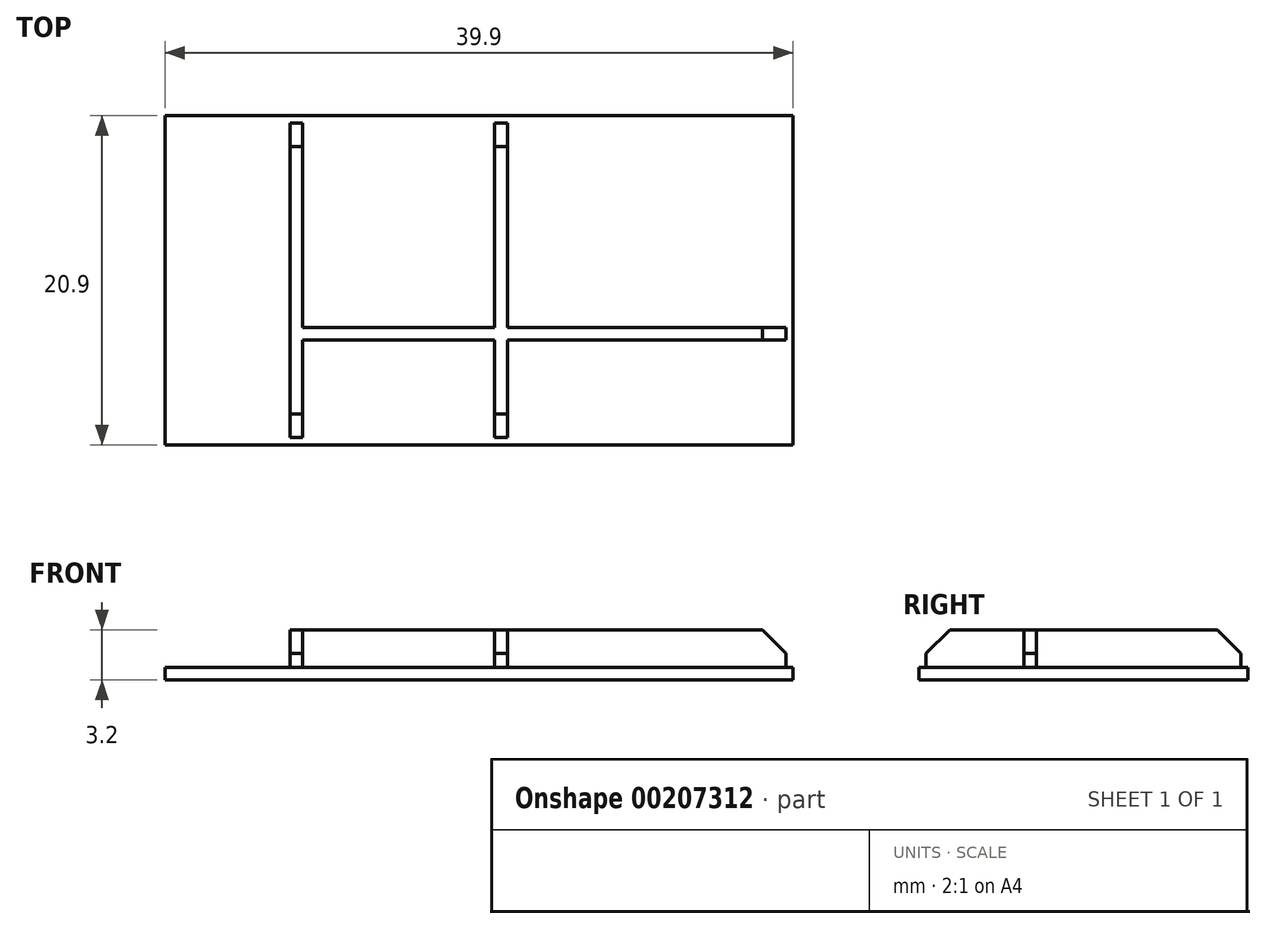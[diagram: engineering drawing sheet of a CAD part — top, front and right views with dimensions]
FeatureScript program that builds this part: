
annotation { "Feature Type Name" : "Feature", "Feature Type Description" : "" }
export const myFeature = defineFeature(function(context is Context, id is Id, definition is map)
    precondition{}
    {
        {
            var Q0;
            Q0=qCreatedBy(makeId("Top.planeOp"),FACE);
            var sketch = newSketch(context, id + "F0", { "sketchPlane" : qUnion([Q0])});
            skLineSegment(sketch, "E0.bottom", {"start": v(19.95, -10.45) * mm, "end": v(-19.95, -10.45) * mm});
            skLineSegment(sketch, "E0.top", {"start": v(19.95, 10.45) * mm, "end": v(-19.95, 10.45) * mm});
            skLineSegment(sketch, "E0.left", {"start": v(19.95, -10.45) * mm, "end": v(19.95, 10.45) * mm});
            skLineSegment(sketch, "E0.right", {"start": v(-19.95, -10.45) * mm, "end": v(-19.95, 10.45) * mm});
            skPoint(sketch, "E0.middle", {"position": v(0, 0) * mm});
            skSolve(sketch);
        }
        {
            var Q0;
            Q0 = qSketchRegion(id + "F0", true);
            extrude(context, id + "F1", {"entities" : qUnion([Q0]), "depth" : .8 * mm});
        }
        {
            var Q0;
            Q0=makeQuery(id+"F1.opExtrude","CAP_FACE",FACE,{"disambiguationData":[OSD([sQuery(id+"F0.wireOp",EDGE,"E0.bottom"),sQuery(id+"F0.wireOp",EDGE,"E0.top"),sQuery(id+"F0.wireOp",EDGE,"E0.left"),sQuery(id+"F0.wireOp",EDGE,"E0.right")])],"isStart":false});
            var sketch = newSketch(context, id + "F2", { "sketchPlane" : qUnion([Q0])});
            skLineSegment(sketch, "E1.bottom", {"start": v(-11.2, -10) * mm, "end": v(-12, -10) * mm});
            skLineSegment(sketch, "E1.top", {"start": v(-11.2, 10) * mm, "end": v(-12, 10) * mm});
            skLineSegment(sketch, "E1.left", {"start": v(-11.2, -10) * mm, "end": v(-11.2, -3.8) * mm});
            skLineSegment(sketch, "E1.right", {"start": v(-12, -10) * mm, "end": v(-12, 10) * mm});
            skLineSegment(sketch, "E2.bottom", {"start": v(1.8, -10) * mm, "end": v(1, -10) * mm});
            skLineSegment(sketch, "E2.top", {"start": v(1.8, 10) * mm, "end": v(1, 10) * mm});
            skLineSegment(sketch, "E2.left", {"start": v(1.8, -10) * mm, "end": v(1.8, -3.8) * mm});
            skLineSegment(sketch, "E2.right", {"start": v(1, -10) * mm, "end": v(1, -3.8) * mm});
            skLineSegment(sketch, "E3.bottom", {"start": v(-11.2, -3) * mm, "end": v(1, -3) * mm});
            skLineSegment(sketch, "E3.top", {"start": v(-11.2, -3.8) * mm, "end": v(1, -3.8) * mm});
            skLineSegment(sketch, "E3.right", {"start": v(19.5, -3) * mm, "end": v(19.5, -3.8) * mm});
            skLineSegment(sketch, "E4.bottom", {"start": v(19.5, -10) * mm, "end": v(-19.5, -10) * mm, "construction": true});
            skLineSegment(sketch, "E4.top", {"start": v(19.5, 10) * mm, "end": v(-19.5, 10) * mm, "construction": true});
            skLineSegment(sketch, "E4.left", {"start": v(19.5, -10) * mm, "end": v(19.5, 10) * mm, "construction": true});
            skLineSegment(sketch, "E4.right", {"start": v(-19.5, -10) * mm, "end": v(-19.5, 10) * mm, "construction": true});
            skPoint(sketch, "E4.middle", {"position": v(0, 0) * mm});
            skLineSegment(sketch, "E5.trimOffspring", {"start": v(-11.2, -3) * mm, "end": v(-11.2, 10) * mm});
            skLineSegment(sketch, "E6.trimOffspring", {"start": v(1, -3) * mm, "end": v(1, 10) * mm});
            skLineSegment(sketch, "E7.trimOffspring", {"start": v(1.8, -3) * mm, "end": v(19.5, -3) * mm});
            skLineSegment(sketch, "E8.trimOffspring", {"start": v(1.8, -3) * mm, "end": v(1.8, 10) * mm});
            skLineSegment(sketch, "E9.trimOffspring", {"start": v(1.8, -3.8) * mm, "end": v(19.5, -3.8) * mm});
            skSolve(sketch);
        }
        {
            var Q0;
            Q0 = qSketchRegion(id + "F2", true);
            extrude(context, id + "F3", {"entities" : qUnion([Q0]), "operationType" : NewBodyOperationType.ADD, "depth" : 2.4 * mm});
        }
        {
            var Q0;
            Q0=makeQuery(id+"F3.opExtrude","CAP_EDGE",EDGE,{"disambiguationData":[OSD([sQuery(id+"F2.wireOp",EDGE,"E1.bottom")])],"isStart":false});
            var Q1;
            Q1=makeQuery(id+"F3.opExtrude","CAP_EDGE",EDGE,{"disambiguationData":[OSD([sQuery(id+"F2.wireOp",EDGE,"E2.bottom")])],"isStart":false});
            var Q2;
            Q2=makeQuery(id+"F3.opExtrude","CAP_EDGE",EDGE,{"disambiguationData":[OSD([sQuery(id+"F2.wireOp",EDGE,"E1.top")])],"isStart":false});
            var Q3;
            Q3=makeQuery(id+"F3.opExtrude","CAP_EDGE",EDGE,{"disambiguationData":[OSD([sQuery(id+"F2.wireOp",EDGE,"E2.top")])],"isStart":false});
            var Q4;
            Q4=makeQuery(id+"F3.opExtrude","CAP_EDGE",EDGE,{"disambiguationData":[OSD([sQuery(id+"F2.wireOp",EDGE,"E3.right")])],"isStart":false});
            chamfer(context, id + "F4", {"entities" : qUnion([Q0, Q1, Q2, Q3, Q4]), "width" : 1.5 * mm, "tangentPropagation" : true});
        }
    });
